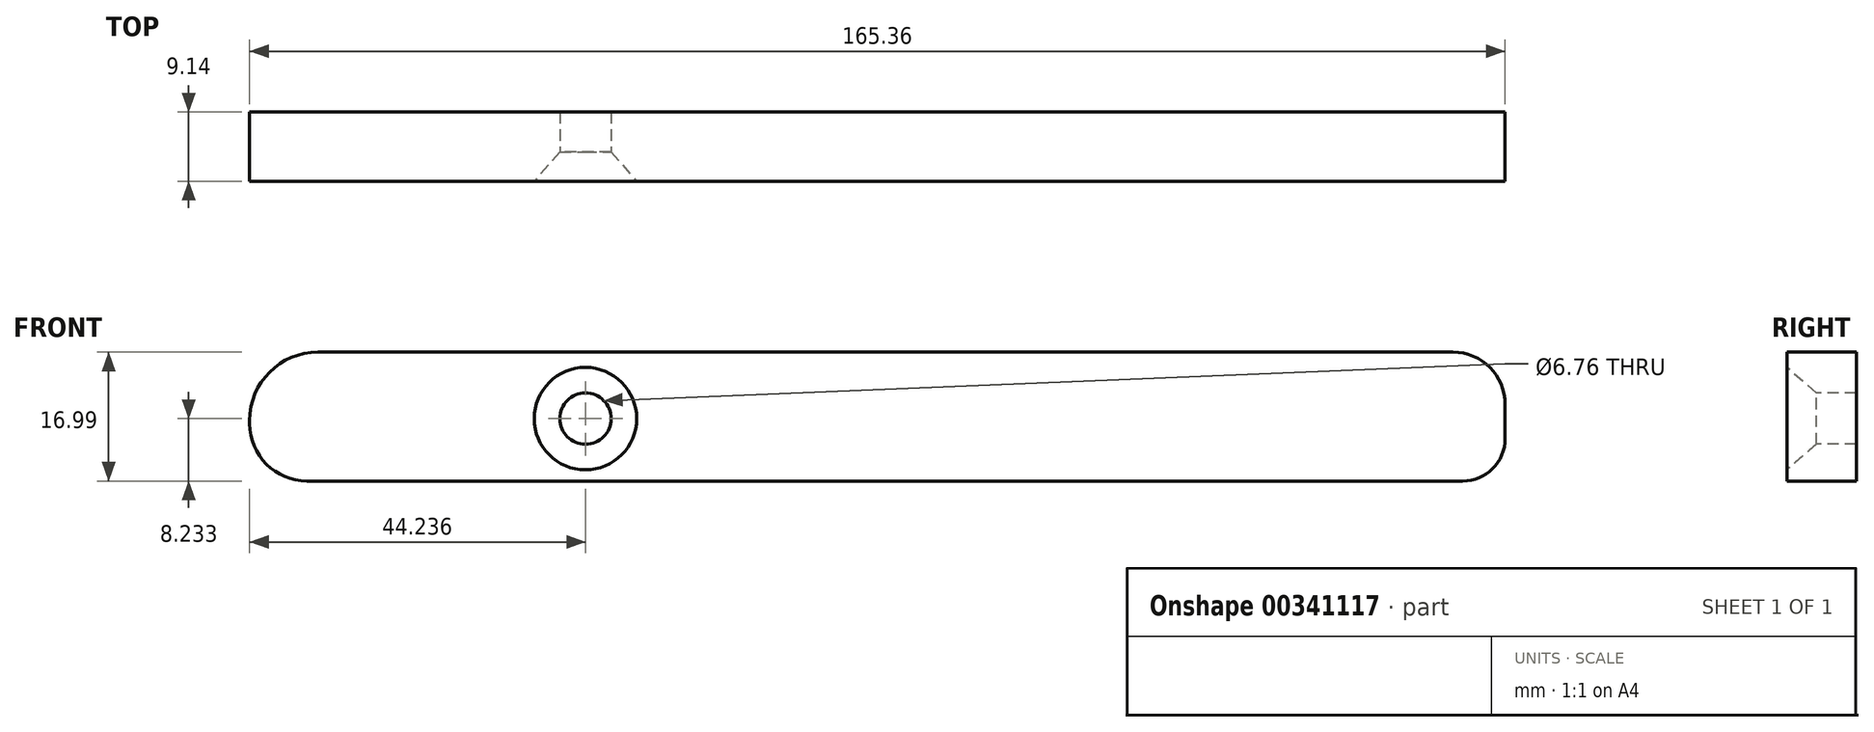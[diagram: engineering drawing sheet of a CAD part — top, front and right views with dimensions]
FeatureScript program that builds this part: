
annotation { "Feature Type Name" : "Feature", "Feature Type Description" : "" }
export const myFeature = defineFeature(function(context is Context, id is Id, definition is map)
    precondition{}
    {
        {
            var Q0;
            Q0=qCreatedBy(makeId("Front.planeOp"),FACE);
            var sketch = newSketch(context, id + "F0", { "sketchPlane" : qUnion([Q0])});
            skLineSegment(sketch, "E0.bottom", {"start": v(-47.13, 42.96) * mm, "end": v(102.35, 42.96) * mm});
            skLineSegment(sketch, "E0.top", {"start": v(-48.56, 25.97) * mm, "end": v(103.62, 25.97) * mm});
            skLineSegment(sketch, "E0.left", {"start": v(-56.13, 33.96) * mm, "end": v(-56.13, 33.54) * mm});
            skLineSegment(sketch, "E0.right", {"start": v(109.23, 36.08) * mm, "end": v(109.23, 31.58) * mm});
            skPoint(sketch, "E1.visualSharp", {"position": v(109.23, 42.96) * mm});
            skArc(sketch, "E1.filletArc", {"start": v(109.23, 36.08) * mm, "mid": v(107.21, 40.95) * mm, "end": v(102.35, 42.96) * mm});
            skPoint(sketch, "E2.visualSharp", {"position": v(109.23, 25.97) * mm});
            skArc(sketch, "E2.filletArc", {"start": v(103.62, 25.97) * mm, "mid": v(107.59, 27.61) * mm, "end": v(109.23, 31.58) * mm});
            skPoint(sketch, "E3.visualSharp", {"position": v(-56.13, 42.96) * mm});
            skArc(sketch, "E3.filletArc", {"start": v(-47.13, 42.96) * mm, "mid": v(-53.5, 40.32) * mm, "end": v(-56.13, 33.96) * mm});
            skPoint(sketch, "E4.visualSharp", {"position": v(-56.13, 25.97) * mm});
            skArc(sketch, "E4.filletArc", {"start": v(-56.13, 33.54) * mm, "mid": v(-53.91, 28.19) * mm, "end": v(-48.56, 25.97) * mm});
            skSolve(sketch);
        }
        {
            var Q0;
            Q0=makeQuery(id+"F0.imprint","IMPRINT",FACE,{"disambiguationData":[TD([[makeQuery(id+"F0.imprint","IMPRINT",EDGE,{"derivedFrom":sQuery(id+"F0.wireOp",EDGE,"E0.bottom")}),-1.0]])]});
            extrude(context, id + "F1", {"entities" : qUnion([Q0]), "depth" : 9.14 * mm});
        }
        {
            var Q0;
            Q0=makeQuery(id+"F1.opExtrude","CAP_FACE",FACE,{"disambiguationData":[OSD([sQuery(id+"F0.wireOp",EDGE,"E0.bottom"),sQuery(id+"F0.wireOp",EDGE,"E0.top"),sQuery(id+"F0.wireOp",EDGE,"E0.left"),sQuery(id+"F0.wireOp",EDGE,"E0.right"),sQuery(id+"F0.wireOp",EDGE,"E1.filletArc"),sQuery(id+"F0.wireOp",EDGE,"E2.filletArc"),sQuery(id+"F0.wireOp",EDGE,"E3.filletArc"),sQuery(id+"F0.wireOp",EDGE,"E4.filletArc")])],"isStart":false});
            var sketch = newSketch(context, id + "F2", { "sketchPlane" : qUnion([Q0])});
            skCircle(sketch, "E5", {"center": v(-11.9, 34.2) * mm, "radius": 5.2 * mm});
            skSolve(sketch);
        }
        {
            var Q0;
            Q0=sQuery(id+"F2.wireOp",VERTEX,"E5.center");
            var Q1;
            Q1=makeQuery(id+"F1.opExtrude","SWEPT_BODY",BODY,{"disambiguationData":[OSD([sQuery(id+"F0.wireOp",EDGE,"E0.bottom"),sQuery(id+"F0.wireOp",EDGE,"E0.top"),sQuery(id+"F0.wireOp",EDGE,"E0.left"),sQuery(id+"F0.wireOp",EDGE,"E0.right"),sQuery(id+"F0.wireOp",EDGE,"E1.filletArc"),sQuery(id+"F0.wireOp",EDGE,"E2.filletArc"),sQuery(id+"F0.wireOp",EDGE,"E3.filletArc"),sQuery(id+"F0.wireOp",EDGE,"E4.filletArc")])]});
            hole(context, id + "F3", {"style" : HoleStyle.C_SINK, "endStyle" : HoleEndStyle.THROUGH, "standardTappedOrClearance" : lookupTablePath({ "standard" : "ANSI", "fit" : "Normal (ASME)", "size" : "1/4", "type" : "Clearance" }), "standardBlindInLast" : lookupTablePath({ "fit" : "Free", "standard" : "ANSI", "size" : "1/4", "type" : "Clearance" }), "holeDiameter" : 6.76 * mm, "cSinkDiameter" : 13.5 * mm, "cSinkAngle" : 82 * degree, "tappedDepth" : 12.7 * mm, "tapClearance" : 3, "locations" : qUnion([Q0]), "scope" : qUnion([Q1])});
        }
    });
